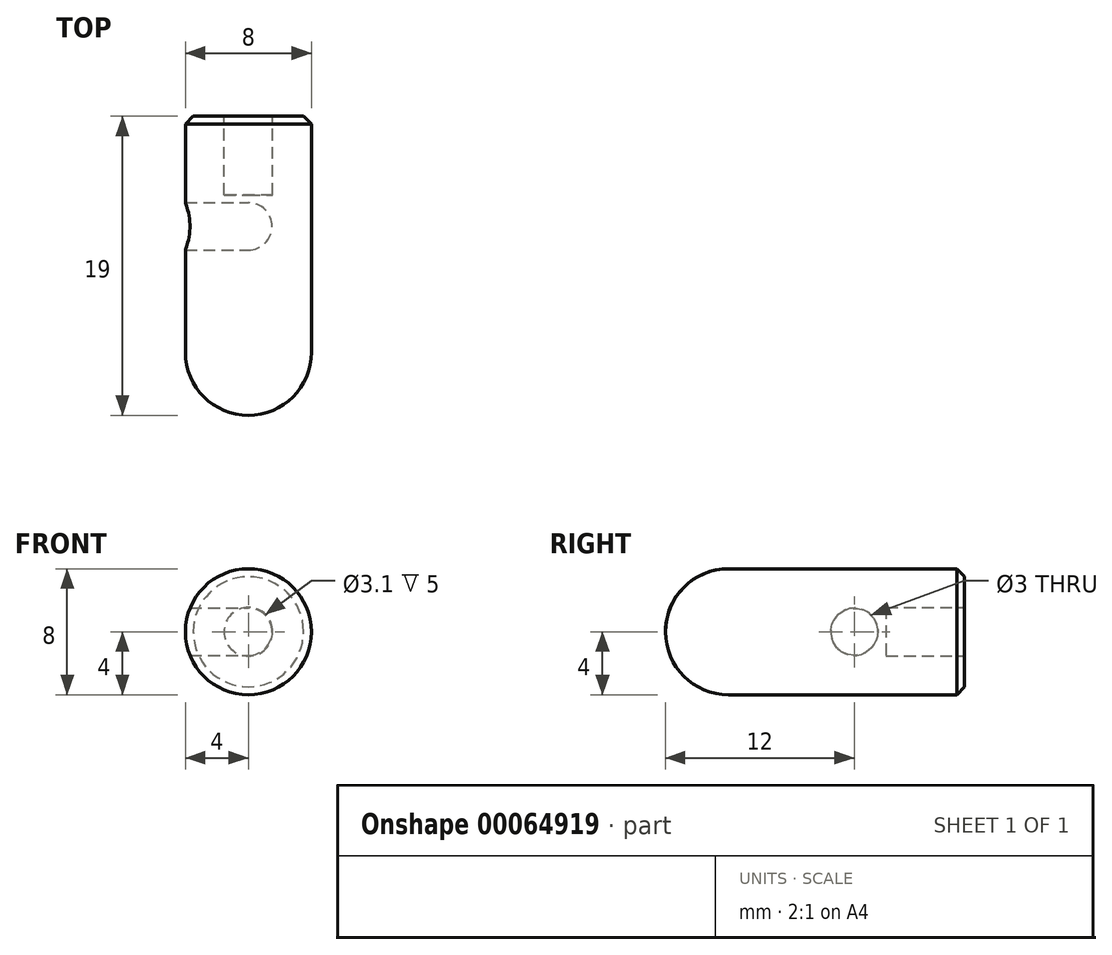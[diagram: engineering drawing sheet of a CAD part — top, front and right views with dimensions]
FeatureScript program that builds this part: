
annotation { "Feature Type Name" : "Feature", "Feature Type Description" : "" }
export const myFeature = defineFeature(function(context is Context, id is Id, definition is map)
    precondition{}
    {
        {
            var Q0;
            Q0=qCreatedBy(makeId("Right.planeOp"),FACE);
            var sketch = newSketch(context, id + "F0", { "sketchPlane" : qUnion([Q0])});
            skLineSegment(sketch, "E0", {"start": v(7, 0) * mm, "end": v(-12, 0) * mm});
            skLineSegment(sketch, "E1.0", {"start": v(7, 4) * mm, "end": v(-8, 4) * mm});
            skPoint(sketch, "E2.orphan", {"position": v(0, 4) * mm});
            skPoint(sketch, "E3.orphan", {"position": v(0, -4) * mm});
            skArc(sketch, "E4", {"start": v(-8, 4) * mm, "mid": v(-10.83, 2.83) * mm, "end": v(-12, 0) * mm});
            skPoint(sketch, "E5.orphan", {"position": v(-45.01, 4) * mm});
            skPoint(sketch, "E6.orphan", {"position": v(-45.01, -4) * mm});
            skLineSegment(sketch, "E7.0", {"start": v(7, 0) * mm, "end": v(7, 4) * mm});
            skCircle(sketch, "E8", {"center": v(0, 0) * mm, "radius": 1.5 * mm});
            skSolve(sketch);
        }
        {
            var Q0;
            Q0 = qSketchRegion(id + "F0", true);
            var Q1;
            Q1=sQuery(id+"F0.wireOp",EDGE,"E0");
            revolve(context, id + "F1", {"entities" : qUnion([Q0]), "axis" : qUnion([Q1]), "revolveType" : RevolveType.FULL});
        }
        {
            var Q0;
            {var subQ0=sQuery(id+"F0.wireOp",EDGE,"E8");var subQ1=sQuery(id+"F0.wireOp",EDGE,"E0");var subQ2=makeQuery(id+"F0.imprint","INTERSECT",VERTEX,{"disambiguationData":[OD(0.0)],"derivedFrom":[subQ1,subQ0]});Q0=makeQuery(id+"F0.imprint","IMPRINT",FACE,{"disambiguationData":[TD([[makeQuery(id+"F0.imprint","IMPRINT",EDGE,{"disambiguationData":[TD([[subQ2,-1.0]])],"derivedFrom":subQ1}),-1.0]])]});}
            var Q1;
            {var subQ0=sQuery(id+"F0.wireOp",EDGE,"E8");var subQ1=sQuery(id+"F0.wireOp",EDGE,"E0");var subQ2=makeQuery(id+"F0.imprint","INTERSECT",VERTEX,{"disambiguationData":[OD(0.0)],"derivedFrom":[subQ1,subQ0]});Q1=makeQuery(id+"F0.imprint","IMPRINT",FACE,{"disambiguationData":[TD([[makeQuery(id+"F0.imprint","IMPRINT",EDGE,{"disambiguationData":[TD([[subQ2,-1.0]])],"derivedFrom":subQ1}),1.0]])]});}
            extrude(context, id + "F2", {"entities" : qUnion([Q0, Q1]), "operationType" : NewBodyOperationType.REMOVE, "oppositeDirection" : true, "depth" : 25 * mm});
        }
        {
            var Q0;
            Q0=makeQuery(id+"F1.opRevolve","SWEPT_EDGE",EDGE,{"disambiguationData":[OSD([sQuery(id+"F0.wireOp",EDGE,"E1.0"),sQuery(id+"F0.wireOp",EDGE,"E7.0")])]});
            chamfer(context, id + "F3", {"entities" : qUnion([Q0]), "width" : 0.5 * mm, "tangentPropagation" : true});
        }
        {
            var Q0;
            Q0=makeQuery(id+"F1.opRevolve","SWEPT_FACE",FACE,{"disambiguationData":[OSD([sQuery(id+"F0.wireOp",EDGE,"E7.0")])]});
            var sketch = newSketch(context, id + "F4", { "sketchPlane" : qUnion([Q0])});
            skCircle(sketch, "E9", {"center": v(0, 0) * mm, "radius": 1.55 * mm});
            skSolve(sketch);
        }
        {
            var Q0;
            Q0 = qSketchRegion(id + "F4", true);
            extrude(context, id + "F5", {"entities" : qUnion([Q0]), "operationType" : NewBodyOperationType.REMOVE, "flatOperationType" : FlatOperationType.REMOVE, "oppositeDirection" : true, "offsetDistance" : 25 * mm, "depth" : 5 * mm, "domain" : OperationDomain.MODEL});
        }
    });
